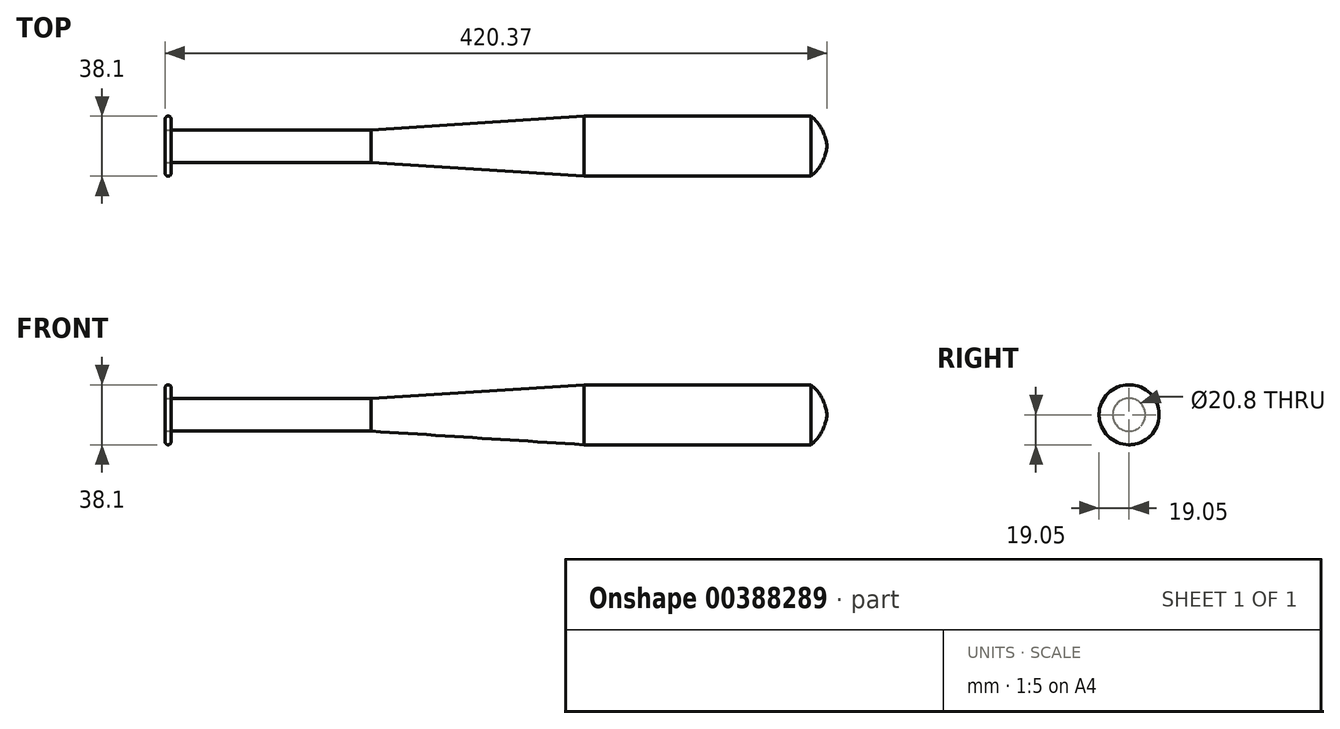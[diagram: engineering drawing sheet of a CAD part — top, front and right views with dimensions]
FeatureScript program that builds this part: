
annotation { "Feature Type Name" : "Feature", "Feature Type Description" : "" }
export const myFeature = defineFeature(function(context is Context, id is Id, definition is map)
    precondition{}
    {
        {
            var Q0;
            Q0=qCreatedBy(makeId("Right.planeOp"),FACE);
            var sketch = newSketch(context, id + "F0", { "sketchPlane" : qUnion([Q0])});
            skCircle(sketch, "E0", {"center": v(0, 0) * mm, "radius": 19.05 * mm});
            skSolve(sketch);
        }
        {
            var Q0;
            Q0=makeQuery(id+"F0.imprint","IMPRINT",FACE,{"disambiguationData":[TD([[makeQuery(id+"F0.imprint","IMPRINT",EDGE,{"derivedFrom":sQuery(id+"F0.wireOp",EDGE,"E0")}),1.0]])]});
            extrude(context, id + "F1", {"entities" : qUnion([Q0]), "endBound" : BoundingType.SYMMETRIC, "depth" : 279.4 * mm});
        }
        {
            var Q0;
            Q0=qCreatedBy(makeId("Front.planeOp"),FACE);
            var sketch = newSketch(context, id + "F2", { "sketchPlane" : qUnion([Q0])});
            skLineSegment(sketch, "E1", {"start": v(-147.22, 26.17) * mm, "end": v(-147.22, 9.92) * mm});
            skLineSegment(sketch, "E2", {"start": v(-147.22, 9.92) * mm, "end": v(20.45, 20.65) * mm});
            skLineSegment(sketch, "E3", {"start": v(-147.22, 26.17) * mm, "end": v(20.45, 20.65) * mm});
            skSolve(sketch);
        }
        {
            var Q0;
            Q0 = qSketchRegion(id + "F2", true);
            var Q1;
            Q1=makeQuery(id+"F1.opExtrude","SWEPT_FACE",FACE,{"disambiguationData":[OSD([sQuery(id+"F0.wireOp",EDGE,"E0")])]});
            revolve(context, id + "F3", {"operationType" : NewBodyOperationType.REMOVE, "entities" : qUnion([Q0]), "axis" : qUnion([Q1]), "revolveType" : RevolveType.FULL, "oppositeDirection" : true});
        }
        {
            var Q0;
            Q0=qCreatedBy(makeId("Front.planeOp"),FACE);
            var sketch = newSketch(context, id + "F4", { "sketchPlane" : qUnion([Q0])});
            skArc(sketch, "E4", {"start": v(139.7, -19.05) * mm, "mid": v(146.69, -10.54) * mm, "end": v(149.86, 0) * mm});
            skLineSegment(sketch, "E5", {"start": v(139.7, 0) * mm, "end": v(139.7, -19.05) * mm});
            skLineSegment(sketch, "E6", {"start": v(139.7, 0) * mm, "end": v(149.86, 0) * mm});
            skSolve(sketch);
        }
        {
            var Q0;
            Q0=makeQuery(id+"F4.imprint","IMPRINT",FACE,{"disambiguationData":[TD([[makeQuery(id+"F4.imprint","IMPRINT",EDGE,{"derivedFrom":sQuery(id+"F4.wireOp",EDGE,"E4")}),1.0]])]});
            var Q1;
            Q1=makeQuery(id+"F1.opExtrude","SWEPT_FACE",FACE,{"disambiguationData":[OSD([sQuery(id+"F0.wireOp",EDGE,"E0")])]});
            revolve(context, id + "F5", {"operationType" : NewBodyOperationType.ADD, "entities" : qUnion([Q0]), "axis" : qUnion([Q1]), "revolveType" : RevolveType.FULL});
        }
        {
            var Q0;
            Q0=makeQuery(id+"F1.opExtrude","CAP_FACE",FACE,{"disambiguationData":[OSD([sQuery(id+"F0.wireOp",EDGE,"E0")])],"isStart":true});
            extrude(context, id + "F6", {"entities" : qUnion([Q0]), "depth" : 127 * mm});
        }
        {
            var Q0;
            Q0=makeQuery(id+"F6.opExtrude","CAP_FACE",FACE,{"disambiguationData":[OSD([sQuery(id+"F0.wireOp",EDGE,"E0")])],"isStart":false});
            var sketch = newSketch(context, id + "F7", { "sketchPlane" : qUnion([Q0])});
            skCircle(sketch, "E7", {"center": v(0, 0) * mm, "radius": 19.05 * mm});
            skSolve(sketch);
        }
        {
            var Q0;
            Q0=makeQuery(id+"F7.imprint","IMPRINT",FACE,{"disambiguationData":[TD([[makeQuery(id+"F7.imprint","IMPRINT",EDGE,{"derivedFrom":sQuery(id+"F7.wireOp",EDGE,"E7")}),1.0]])]});
            extrude(context, id + "F8", {"entities" : qUnion([Q0]), "depth" : 3.8 * mm});
        }
        {
            var Q0;
            Q0=makeQuery(id+"F8.opExtrude","CAP_EDGE",EDGE,{"disambiguationData":[OSD([sQuery(id+"F7.wireOp",EDGE,"E7")])],"isStart":false});
            fillet(context, id + "F9", {"entities" : qUnion([Q0]), "radius" : 1.9 * mm, "tangentPropagation" : true, "allowEdgeOverflow" : false});
        }
        {
            var Q0;
            Q0=makeQuery(id+"F8.opExtrude","CAP_EDGE",EDGE,{"disambiguationData":[OSD([sQuery(id+"F7.wireOp",EDGE,"E7")])],"isStart":true});
            fillet(context, id + "F10", {"entities" : qUnion([Q0]), "radius" : 1.9 * mm, "tangentPropagation" : true, "allowEdgeOverflow" : false});
        }
        {
            var Q0;
            Q0=makeQuery(id+"F6.opExtrude","CAP_FACE",FACE,{"disambiguationData":[OSD([sQuery(id+"F0.wireOp",EDGE,"E0")])],"isStart":false});
            var Q1;
            Q1=makeQuery(id+"F8.opExtrude","CAP_FACE",FACE,{"disambiguationData":[OSD([sQuery(id+"F0.wireOp",EDGE,"E0"),sQuery(id+"F2.wireOp",EDGE,"E2"),sQuery(id+"F7.wireOp",EDGE,"E7")])],"isStart":false});
            extrude(context, id + "F11", {"entities" : qUnion([Q0]), "endBound" : BoundingType.UP_TO_SURFACE, "endBoundEntityFace" : qUnion([Q1]), "depth" : 4.32 * mm});
        }
    });
